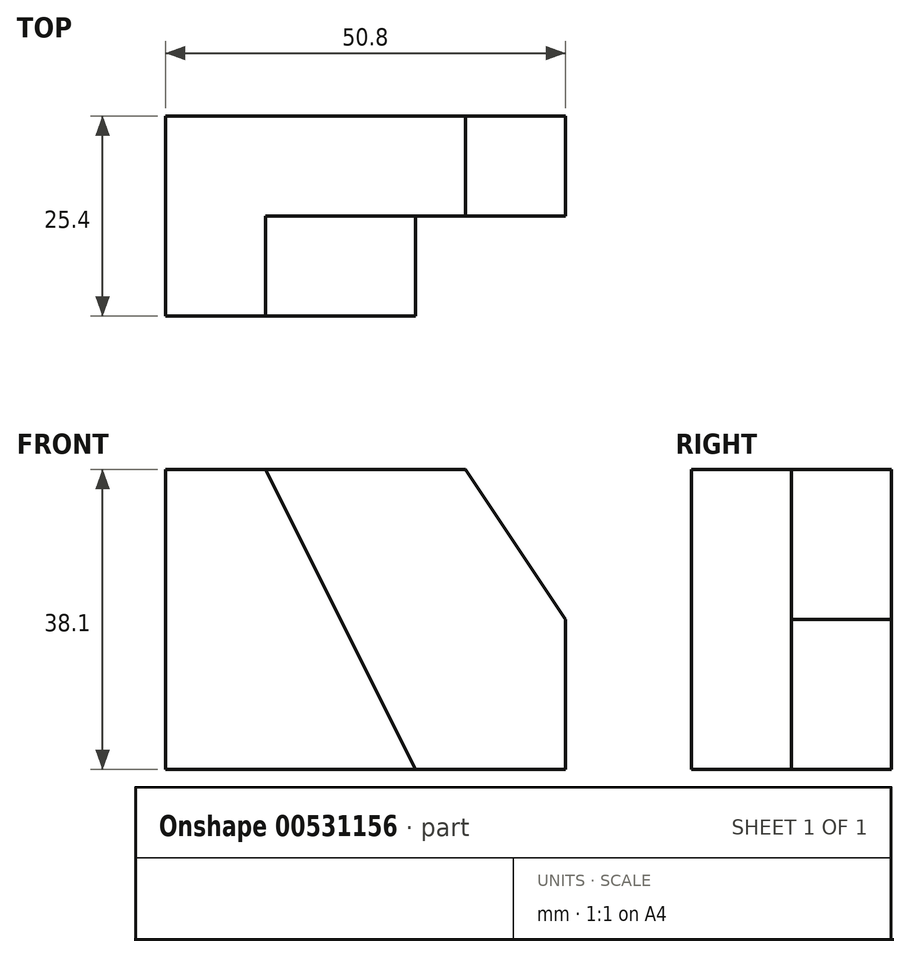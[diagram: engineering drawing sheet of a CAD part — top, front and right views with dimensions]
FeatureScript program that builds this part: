
annotation { "Feature Type Name" : "Feature", "Feature Type Description" : "" }
export const myFeature = defineFeature(function(context is Context, id is Id, definition is map)
    precondition{}
    {
        {
            var Q0;
            Q0=qCreatedBy(makeId("Front.planeOp"),FACE);
            var sketch = newSketch(context, id + "F0", { "sketchPlane" : qUnion([Q0])});
            skLineSegment(sketch, "E0.bottom", {"start": v(0, 0) * mm, "end": v(50.8, 0) * mm});
            skLineSegment(sketch, "E0.top", {"start": v(0, 38.1) * mm, "end": v(50.8, 38.1) * mm});
            skLineSegment(sketch, "E0.left", {"start": v(0, 0) * mm, "end": v(0, 38.1) * mm});
            skLineSegment(sketch, "E0.right", {"start": v(50.8, 0) * mm, "end": v(50.8, 38.1) * mm});
            skSolve(sketch);
        }
        {
            var Q0;
            Q0 = qSketchRegion(id + "F0", true);
            extrude(context, id + "F1", {"entities" : qUnion([Q0]), "depth" : 25.4 * mm, "offsetDistance" : 25.4 * mm});
        }
        {
            var Q0;
            Q0=makeQuery(id+"F1.opExtrude","CAP_FACE",FACE,{"disambiguationData":[OSD([sQuery(id+"F0.wireOp",EDGE,"E0.bottom"),sQuery(id+"F0.wireOp",EDGE,"E0.top"),sQuery(id+"F0.wireOp",EDGE,"E0.left"),sQuery(id+"F0.wireOp",EDGE,"E0.right")])],"isStart":false});
            var sketch = newSketch(context, id + "F2", { "sketchPlane" : qUnion([Q0])});
            skLineSegment(sketch, "E1", {"start": v(0, 38.1) * mm, "end": v(12.7, 38.1) * mm, "construction": true});
            skLineSegment(sketch, "E2", {"start": v(50.8, 0) * mm, "end": v(31.75, 0) * mm, "construction": true});
            skLineSegment(sketch, "E3", {"start": v(31.75, 0) * mm, "end": v(12.7, 38.1) * mm, "construction": true});
            skLineSegment(sketch, "E4", {"start": v(12.7, 38.1) * mm, "end": v(31.75, 0) * mm});
            skLineSegment(sketch, "E5", {"start": v(31.75, 0) * mm, "end": v(50.8, 0) * mm});
            skLineSegment(sketch, "E6", {"start": v(50.8, 0) * mm, "end": v(50.8, 38.1) * mm});
            skLineSegment(sketch, "E7", {"start": v(12.7, 38.1) * mm, "end": v(50.8, 38.1) * mm});
            skSolve(sketch);
        }
        {
            var Q0;
            Q0=makeQuery(id+"F2.imprint","IMPRINT",FACE,{"disambiguationData":[TD([[makeQuery(id+"F2.imprint","IMPRINT",EDGE,{"derivedFrom":sQuery(id+"F2.wireOp",EDGE,"E4")}),1.0]])]});
            extrude(context, id + "F3", {"entities" : qUnion([Q0]), "operationType" : NewBodyOperationType.REMOVE, "oppositeDirection" : true, "depth" : 12.7 * mm, "offsetDistance" : 25.4 * mm});
        }
        {
            var Q0;
            Q0=makeQuery(id+"F1.opExtrude","CAP_FACE",FACE,{"disambiguationData":[OSD([sQuery(id+"F0.wireOp",EDGE,"E0.bottom"),sQuery(id+"F0.wireOp",EDGE,"E0.top"),sQuery(id+"F0.wireOp",EDGE,"E0.left"),sQuery(id+"F0.wireOp",EDGE,"E0.right")])],"isStart":true});
            var sketch = newSketch(context, id + "F4", { "sketchPlane" : qUnion([Q0])});
            skLineSegment(sketch, "E8", {"start": v(-50.8, 38.1) * mm, "end": v(-50.8, 19.05) * mm, "construction": true});
            skLineSegment(sketch, "E9", {"start": v(-50.8, 38.1) * mm, "end": v(-38.1, 38.1) * mm, "construction": true});
            skLineSegment(sketch, "E10", {"start": v(-38.1, 38.1) * mm, "end": v(-50.8, 19.05) * mm});
            skLineSegment(sketch, "E11", {"start": v(-38.1, 38.1) * mm, "end": v(-50.8, 38.1) * mm});
            skLineSegment(sketch, "E12", {"start": v(-50.8, 19.05) * mm, "end": v(-50.8, 38.1) * mm});
            skSolve(sketch);
        }
        {
            var Q0;
            Q0 = qSketchRegion(id + "F4", true);
            extrude(context, id + "F5", {"entities" : qUnion([Q0]), "operationType" : NewBodyOperationType.REMOVE, "oppositeDirection" : true, "depth" : 25.4 * mm, "offsetDistance" : 25.4 * mm});
        }
    });
